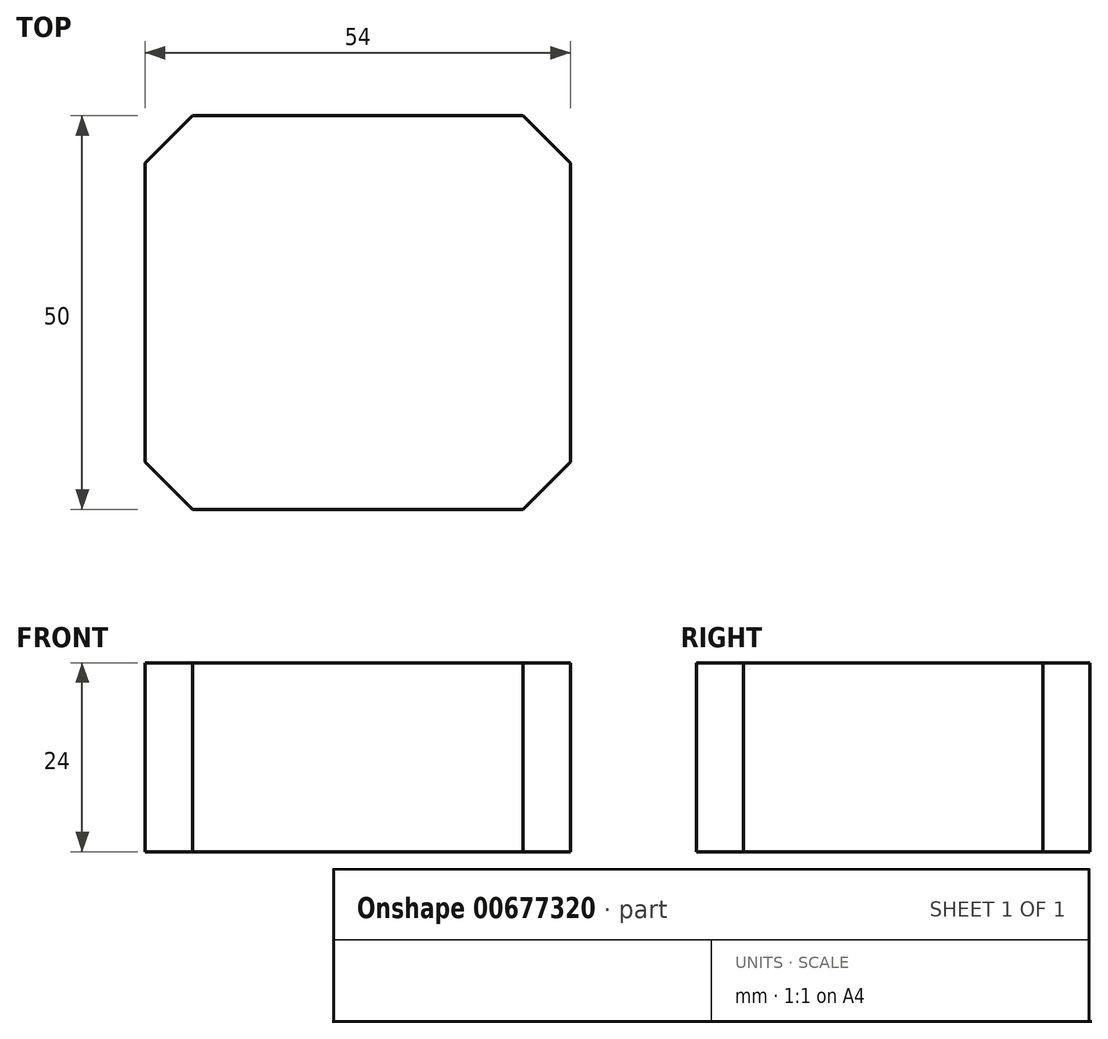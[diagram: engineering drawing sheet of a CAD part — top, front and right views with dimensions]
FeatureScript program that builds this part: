
annotation { "Feature Type Name" : "Feature", "Feature Type Description" : "" }
export const myFeature = defineFeature(function(context is Context, id is Id, definition is map)
    precondition{}
    {
        {
            var Q0;
            Q0=qCreatedBy(makeId("Top.planeOp"),FACE);
            var sketch = newSketch(context, id + "F0", { "sketchPlane" : qUnion([Q0])});
            skLineSegment(sketch, "E0.bottom", {"start": v(27, 25) * mm, "end": v(-27, 25) * mm});
            skLineSegment(sketch, "E0.top", {"start": v(27, -25) * mm, "end": v(-27, -25) * mm});
            skLineSegment(sketch, "E0.left", {"start": v(27, 25) * mm, "end": v(27, -25) * mm});
            skLineSegment(sketch, "E0.right", {"start": v(-27, 25) * mm, "end": v(-27, -25) * mm});
            skPoint(sketch, "E0.middle", {"position": v(0, 0) * mm});
            skSolve(sketch);
        }
        {
            var Q0;
            Q0=makeQuery(id+"F0.imprint","IMPRINT",FACE,{"disambiguationData":[TD([[makeQuery(id+"F0.imprint","IMPRINT",EDGE,{"derivedFrom":sQuery(id+"F0.wireOp",EDGE,"E0.bottom")}),1.0]])]});
            extrude(context, id + "F1", {"entities" : qUnion([Q0]), "depth" : 24 * mm, "offsetDistance" : 25 * mm});
        }
        {
            var Q0;
            Q0=makeQuery(id+"F1.opExtrude","SWEPT_EDGE",EDGE,{"disambiguationData":[OSD([sQuery(id+"F0.wireOp",EDGE,"E0.bottom"),sQuery(id+"F0.wireOp",EDGE,"E0.right")])]});
            var Q1;
            Q1=makeQuery(id+"F1.opExtrude","SWEPT_EDGE",EDGE,{"disambiguationData":[OSD([sQuery(id+"F0.wireOp",EDGE,"E0.bottom"),sQuery(id+"F0.wireOp",EDGE,"E0.left")])]});
            var Q2;
            Q2=makeQuery(id+"F1.opExtrude","SWEPT_EDGE",EDGE,{"disambiguationData":[OSD([sQuery(id+"F0.wireOp",EDGE,"E0.top"),sQuery(id+"F0.wireOp",EDGE,"E0.left")])]});
            var Q3;
            Q3=makeQuery(id+"F1.opExtrude","SWEPT_EDGE",EDGE,{"disambiguationData":[OSD([sQuery(id+"F0.wireOp",EDGE,"E0.top"),sQuery(id+"F0.wireOp",EDGE,"E0.right")])]});
            chamfer(context, id + "F2", {"entities" : qUnion([Q0, Q1, Q2, Q3]), "width" : 6 * mm, "tangentPropagation" : true});
        }
    });
